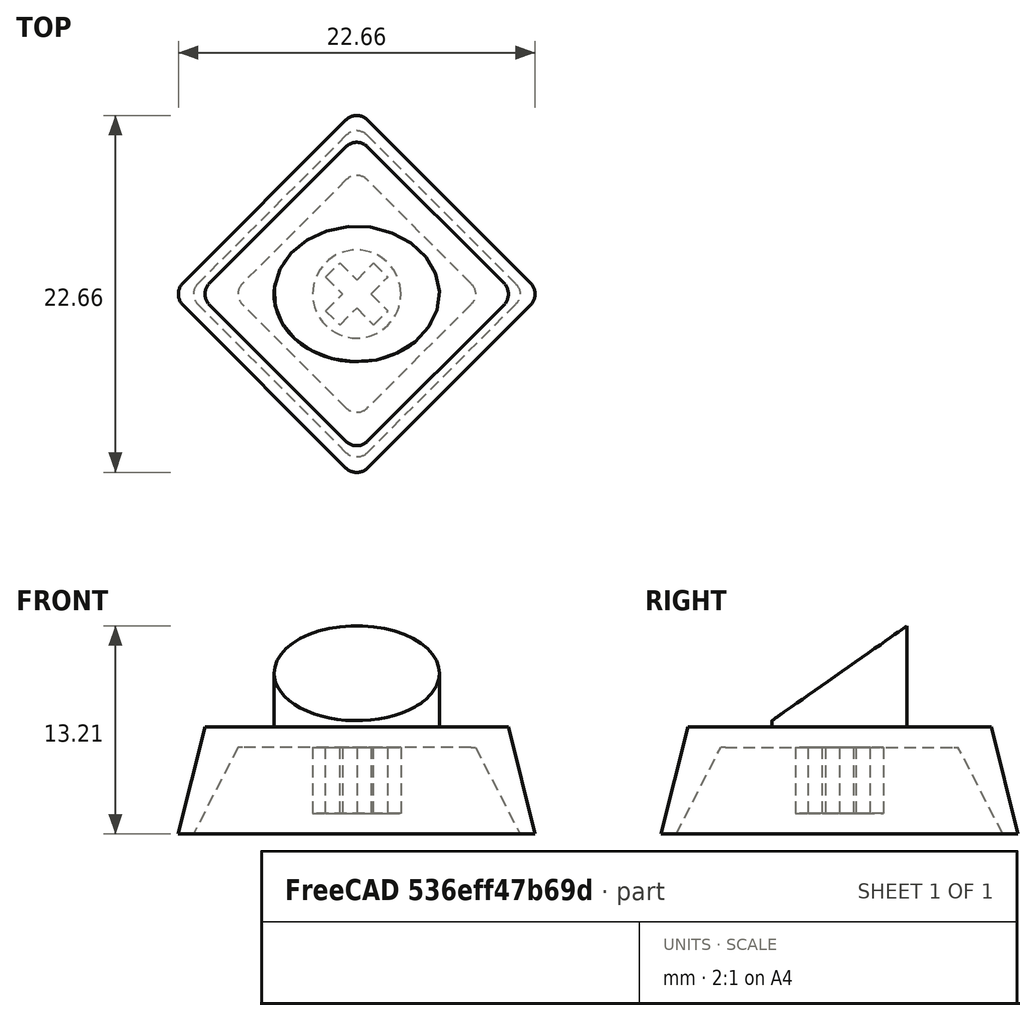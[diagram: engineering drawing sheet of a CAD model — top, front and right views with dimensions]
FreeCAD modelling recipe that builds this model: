
FCSTD DOCUMENT  (FreeCAD 1.0R39319 (Git))
Label: logo_base
License: All rights reserved
LicenseURL: https://en.wikipedia.org/wiki/All_rights_reserved
objects: Part::Cut×5, Part::Box×4, Part::MultiFuse×3, Part::Cylinder×2, Part::Feature×2, Part::Fillet×2, Part::Part2DObjectPython×1, Part::Extrusion×1
note: 20 computed .brp shape members not serialized (recipe doc carries the construction recipe); baked Part::Feature solids carry a one-line shape summary decoded from their .brp

FEATURE [Part::Part2DObjectPython] Circle  # Draft 2D object (typed FeaturePython)
  Area = 86.5901
  FirstAngle = 0
  LastAngle = 0
  MakeFace = true
  Placement = pos=(0,0,10.2) rot=(1,1,0;0.610865rad)
  Radius = 5.25
FEATURE [Part::Box] Box016  label="立方体016"
  AttacherType = Attacher::AttachEngine3D
  Height = 1
  Length = 15.2
  Placement = pos=(-7.6,-7.6,-1) rot=(0,0,1;0rad)
  Width = 15.2
FEATURE [Part::Box] Box017  label="立方体017"
  AttacherType = Attacher::AttachEngine3D
  Height = 1
  Length = 16.6
  Placement = pos=(-8.3,-8.3,-1) rot=(0,0,1;0rad)
  Width = 16.6
FEATURE [Part::Box] Box018  label="立方体018"
  AttacherType = Attacher::AttachEngine3D
  Height = 4.2
  Length = 4.3
  Placement = pos=(-2.15,-0.63,1.3) rot=(0,0,1;0rad)
  Width = 1.27
FEATURE [Part::Box] Box019  label="立方体019"
  AttacherType = Attacher::AttachEngine3D
  Height = 4.2
  Length = 1.27
  Placement = pos=(-0.63,-2.15,1.3) rot=(0,0,1;0rad)
  Width = 4.3
FEATURE [Part::Cylinder] Cylinder002  label="円柱002"
  Angle = 360
  AttacherType = Attacher::AttachEngine3D
  FirstAngle = 0
  Height = 4.2
  Placement = pos=(0,0,1.3) rot=(0,0,1;0rad)
  Radius = 2.8
  SecondAngle = 0
FEATURE [Part::MultiFuse] Fusion006
  Shapes = -> [Box018,Box019]
FEATURE [Part::Cut] Cut012
  Base = -> Cylinder002
  Tool = -> Fusion006
FEATURE [Part::Feature] hull005
  shape: bbox 15.2 x 15.2 x 6.5 mm, 10 faces (baked)
FEATURE [Part::Cut] Cut009
  Base = -> hull005
  Tool = -> Box016
FEATURE [Part::Fillet] Fillet013
  Base = -> Cut009
  EdgeLinks = -> Cut009 [Edge1,Edge3,Edge6,Edge10]
  Edges = 4 edges r=1: [Edge1,Edge3,Edge6,Edge10]
FEATURE [Part::Feature] hull006
  shape: bbox 16.6 x 16.6 x 7.8 mm, 10 faces (baked)
FEATURE [Part::Cut] Cut010
  Base = -> hull006
  Tool = -> Box017
FEATURE [Part::Fillet] Fillet014
  Base = -> Cut010
  EdgeLinks = -> Cut010 [Edge1,Edge3,Edge6,Edge10]
  Edges = 4 edges r=1: [Edge1,Edge3,Edge6,Edge10]
FEATURE [Part::Cut] Cut011
  Base = -> Fillet014
  Tool = -> Fillet013
FEATURE [Part::MultiFuse] Fusion007
  Shapes = -> [Cut012,Cut011]
FEATURE [Part::Extrusion] Extrude
  Base = -> Circle
  Dir = (0,0,-1)
  DirMode = 0
  FaceMakerClass = Part::FaceMakerBullseye
  FaceMakerMode = 3
  LengthFwd = 7
  LengthRev = 0
  Solid = false
  Symmetric = false
FEATURE [Part::Cylinder] Cylinder003  label="円柱003"
  Angle = 360
  AttacherType = Attacher::AttachEngine3D
  FirstAngle = 0
  Height = 6.8
  Radius = 6
  SecondAngle = 0
FEATURE [Part::Cut] Cut013
  Base = -> Extrude
  Tool = -> Cylinder003
FEATURE [Part::MultiFuse] Fusion008  label="logo_base"
  Placement = pos=(0,0,0) rot=(0,0,1;-0.785398rad)
  Shapes = -> [Fusion007,Cut013]
